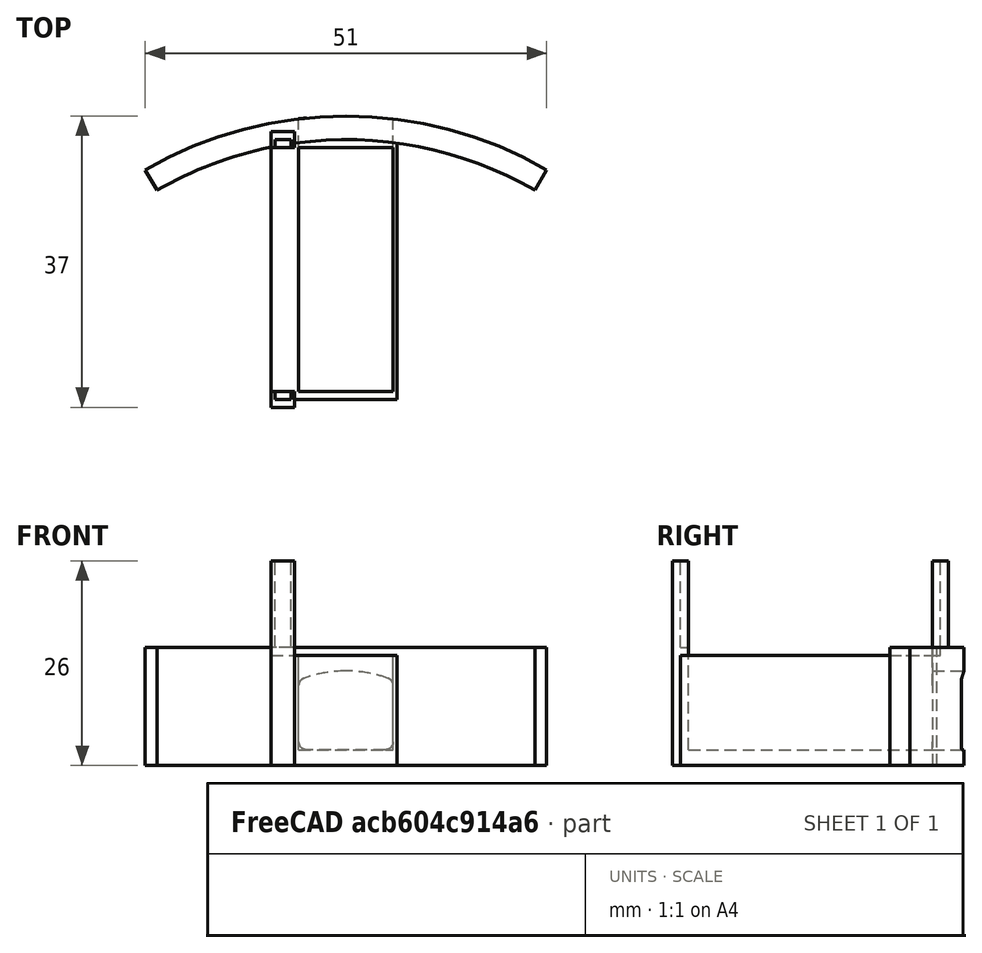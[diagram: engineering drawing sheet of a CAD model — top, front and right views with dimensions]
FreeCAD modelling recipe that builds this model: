
FCSTD DOCUMENT  (FreeCAD 0.16R4924 (Git))
Label: interior_servo_bay_v3p4
License: All rights reserved
LicenseURL: http://en.wikipedia.org/wiki/All_rights_reserved
objects: Part::Cut×5, Part::Box×5, Part::MultiFuse×3, Part::Cylinder×2, Part::Feature×2, Part::Extrusion×2, App::MeasureDistance×2, Part::Thickness×1
note: 20 computed .brp shape members not serialized (recipe doc carries the construction recipe); baked Part::Feature solids carry a one-line shape summary decoded from their .brp

FEATURE [Part::Cylinder] Cylinder  label="bottle_wall"
  Angle = 60
  Height = 15
  Placement = pos=(8.5,-7,0) rot=(0,0,1;1.0472rad)
  Radius = 51
FEATURE [Part::Cylinder] Cylinder001  label="bottle_wall001"
  Angle = 60
  Height = 15
  Placement = pos=(8.5,-7,0) rot=(0,0,1;1.0472rad)
  Radius = 48
FEATURE [Part::Cut] Cut  label="bottle_wall_composite"
  Base = -> Cylinder
  Placement = pos=(0,-2,0) rot=(0,0,1;0rad)
  Tool = -> Cylinder001
FEATURE [Part::Feature] Common_cs  label="pin_cs"
  Placement = pos=(3.5,35,2) rot=(0,0,1;0rad)
  shape: bbox 10 x 2e-07 x 8 mm, 0 faces, 0 solids (baked)
FEATURE [Part::Extrusion] Extrude
  Base = -> Common_cs
  Dir = (0,5,0)
  Solid = true
FEATURE [Part::Thickness] Thickness
  Faces = -> Extrude [Face7]
  Intersection = false
  Join = 0
  Mode = 0
  SelfIntersection = false
  Value = 1
FEATURE [Part::Feature] Common_cs001  label="pin_cs001"
  Placement = pos=(3.5,35,2) rot=(0,0,1;0rad)
  shape: bbox 10 x 2e-07 x 8 mm, 0 faces, 0 solids (baked)
FEATURE [Part::Extrusion] Extrude001
  Base = -> Common_cs001
  Dir = (0,5,0)
  Solid = true
FEATURE [Part::MultiFuse] Fusion  label="bolt_bottle_side_opening"
  Placement = pos=(0,-7,1) rot=(0,0,1;0rad)
  Shapes = -> [Thickness,Extrude,Extrude001]
FEATURE [Part::Box] Box  label="pullBay"
  Height = 15
  Length = 12
  Placement = pos=(2.5,7,2) rot=(0,0,1;0rad)
  Width = 31
FEATURE [Part::Box] Box001  label="Case"
  Height = 14
  Length = 13
  Placement = pos=(2,6,0) rot=(0,0,1;0rad)
  Width = 34
FEATURE [Part::Cut] Cut001  label="cut bay from case"
  Base = -> Box001
  Tool = -> Box
FEATURE [Part::MultiFuse] Fusion001  label="wall plus case"
  Shapes = -> [Cut,Cut001]
FEATURE [Part::Cut] Cut002  label="hole cut out of case"
  Base = -> Fusion001
  Tool = -> Fusion
FEATURE [Part::Box] Box002  label="slot wall"
  Height = 26
  Length = 3
  Placement = pos=(-1,5,0) rot=(0,0,1;0rad)
  Width = 35
FEATURE [Part::Box] Box003  label="slot wall cutout1"
  Height = 11.2
  Length = 2
  Placement = pos=(-0.5,6,15) rot=(0,0,1;0rad)
  Width = 33
FEATURE [Part::Cut] Cut003
  Base = -> Box002
  Tool = -> Box003
FEATURE [Part::Box] Box004  label="slot wall cutout2"
  Height = 14
  Length = 3
  Placement = pos=(-1,7,14) rot=(0,0,1;0rad)
  Width = 31
FEATURE [Part::Cut] Cut004  label="wall slot finished"
  Base = -> Cut003
  Tool = -> Box004
FEATURE [Part::MultiFuse] Fusion002
  Shapes = -> [Cut002,Cut004]
FEATURE [App::MeasureDistance] Distance  label="Distance: 33.123"
  Distance = 33.1232
  P1 = (1.15787,39.1229,26)
  P2 = (1.00961,6,26)
FEATURE [App::MeasureDistance] Distance001  label="Distance: 12.028"
  Distance = 12.0279
  P1 = (0,7,26)
  P2 = (0,7.81869,14)
